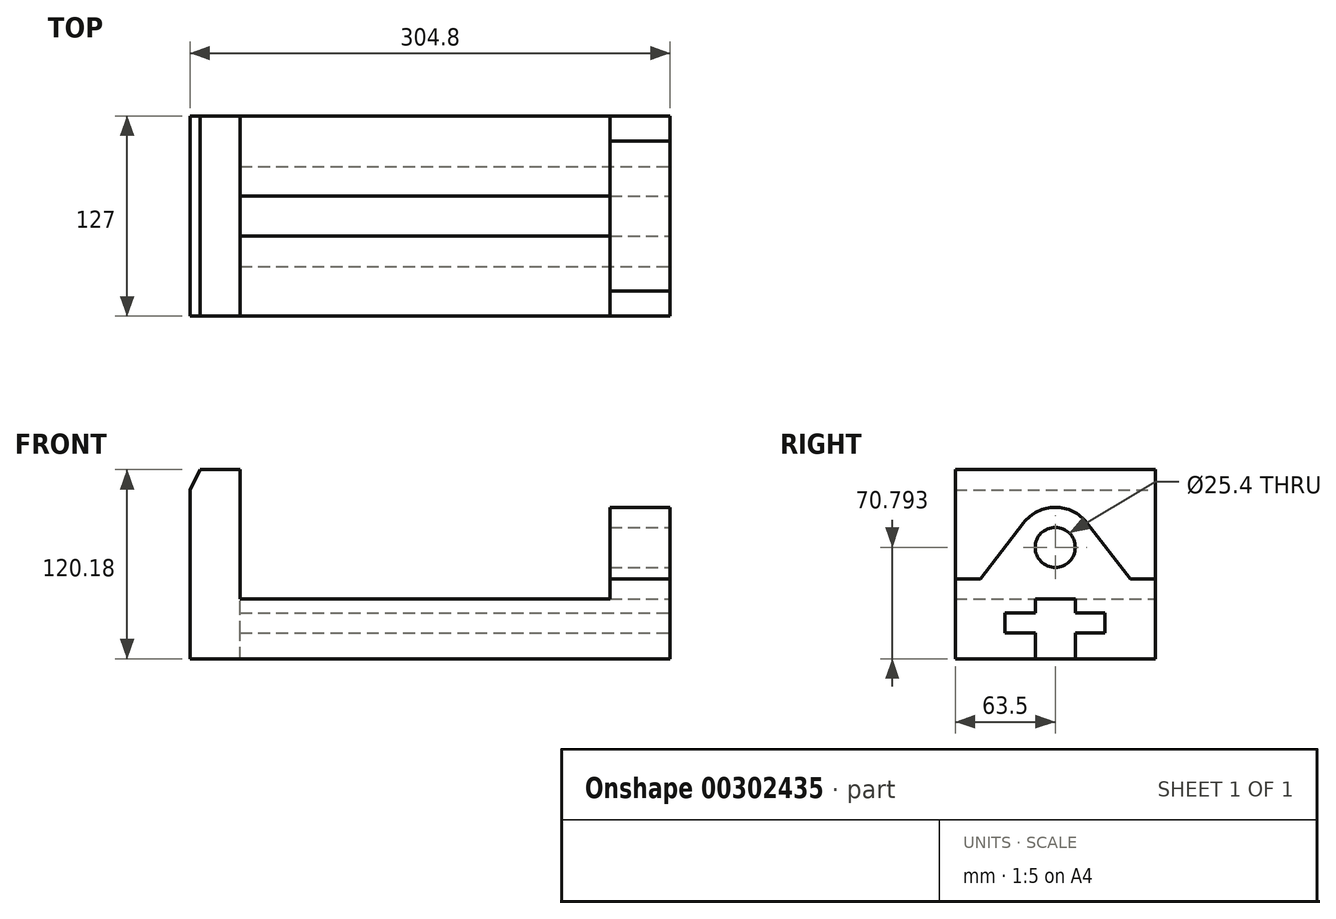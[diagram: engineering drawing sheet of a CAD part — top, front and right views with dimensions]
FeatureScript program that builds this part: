
annotation { "Feature Type Name" : "Feature", "Feature Type Description" : "" }
export const myFeature = defineFeature(function(context is Context, id is Id, definition is map)
    precondition{}
    {
        {
            var Q0;
            Q0=qCreatedBy(makeId("Front.planeOp"),FACE);
            var sketch = newSketch(context, id + "F0", { "sketchPlane" : qUnion([Q0])});
            skLineSegment(sketch, "E0", {"start": v(0, 107.32) * mm, "end": v(0, 0) * mm});
            skLineSegment(sketch, "E1", {"start": v(0, 0) * mm, "end": v(304.8, 0) * mm});
            skLineSegment(sketch, "E2", {"start": v(304.8, 0) * mm, "end": v(304.8, 101.6) * mm});
            skLineSegment(sketch, "E3", {"start": v(304.8, 101.6) * mm, "end": v(266.7, 101.6) * mm});
            skLineSegment(sketch, "E4", {"start": v(266.7, 101.6) * mm, "end": v(266.7, 38.1) * mm});
            skLineSegment(sketch, "E5", {"start": v(266.7, 38.1) * mm, "end": v(31.75, 38.1) * mm});
            skLineSegment(sketch, "E6", {"start": v(31.75, 38.1) * mm, "end": v(31.75, 120.18) * mm});
            skLineSegment(sketch, "E7", {"start": v(31.75, 120.18) * mm, "end": v(6.21, 120.18) * mm});
            skLineSegment(sketch, "E8", {"start": v(6.21, 120.18) * mm, "end": v(0, 107.32) * mm});
            skLineSegment(sketch, "E9", {"start": v(266.7, 60.45) * mm, "end": v(304.8, 60.45) * mm});
            skSolve(sketch);
        }
        {
            var Q0;
            Q0 = qSketchRegion(id + "F0", true);
            extrude(context, id + "F1", {"entities" : qUnion([Q0]), "depth" : 127 * mm});
        }
        {
            var Q0;
            Q0=makeQuery(id+"F1.opExtrude","SWEPT_FACE",FACE,{"disambiguationData":[OSD([sQuery(id+"F0.wireOp",EDGE,"E2")])]});
            var sketch = newSketch(context, id + "F2", { "sketchPlane" : qUnion([Q0])});
            skLineSegment(sketch, "E10", {"start": v(-76.2, 0) * mm, "end": v(-76.2, 16.51) * mm});
            skLineSegment(sketch, "E11", {"start": v(-76.2, 16.51) * mm, "end": v(-95.4, 16.51) * mm});
            skLineSegment(sketch, "E12", {"start": v(-95.4, 16.51) * mm, "end": v(-95.4, 29.21) * mm});
            skLineSegment(sketch, "E13", {"start": v(-95.4, 29.21) * mm, "end": v(-76.2, 29.21) * mm});
            skLineSegment(sketch, "E14", {"start": v(-76.2, 29.21) * mm, "end": v(-76.2, 38.1) * mm});
            skLineSegment(sketch, "E15", {"start": v(-76.2, 38.1) * mm, "end": v(-50.8, 38.1) * mm});
            skLineSegment(sketch, "E16", {"start": v(-50.8, 38.1) * mm, "end": v(-50.8, 29.21) * mm});
            skLineSegment(sketch, "E17", {"start": v(-50.8, 29.21) * mm, "end": v(-31.9, 29.21) * mm});
            skLineSegment(sketch, "E18", {"start": v(-31.9, 29.21) * mm, "end": v(-31.9, 16.51) * mm});
            skLineSegment(sketch, "E19", {"start": v(-31.9, 16.51) * mm, "end": v(-50.8, 16.51) * mm});
            skLineSegment(sketch, "E20", {"start": v(-50.8, 16.51) * mm, "end": v(-50.8, 0) * mm});
            skCircle(sketch, "E21", {"center": v(-63.5, 70.8) * mm, "radius": 12.7 * mm});
            skPoint(sketch, "E21.centerSnap0", {"position": v(-63.5, 38.1) * mm});
            skLineSegment(sketch, "E22", {"start": v(-127, 50.8) * mm, "end": v(-111.13, 50.8) * mm});
            skLineSegment(sketch, "E23", {"start": v(0, 50.8) * mm, "end": v(-15.87, 50.8) * mm});
            skLineSegment(sketch, "E24", {"start": v(-111.12, 50.8) * mm, "end": v(-83.58, 86.35) * mm});
            skLineSegment(sketch, "E25", {"start": v(-15.87, 50.8) * mm, "end": v(-43.42, 86.35) * mm});
            skArc(sketch, "E26", {"start": v(-43.42, 86.35) * mm, "mid": v(-63.5, 96.2) * mm, "end": v(-83.58, 86.35) * mm});
            skSolve(sketch);
        }
        {
            var Q0;
            {var subQ0=sQuery(id+"F2.wireOp",EDGE,"E10");Q0=makeQuery(id+"F2.imprint","IMPRINT",FACE,{"disambiguationData":[TD([[makeQuery(id+"F2.imprint","IMPRINT",EDGE,{"derivedFrom":subQ0}),-1.0]])]});}
            extrude(context, id + "F3", {"entities" : qUnion([Q0]), "operationType" : NewBodyOperationType.REMOVE, "oppositeDirection" : true, "depth" : 273.05 * mm});
        }
        {
            var Q0;
            Q0=makeQuery(id+"F2.imprint","IMPRINT",FACE,{"disambiguationData":[TD([[makeQuery(id+"F2.imprint","IMPRINT",EDGE,{"derivedFrom":sQuery(id+"F2.wireOp",EDGE,"E21")}),1.0]])]});
            var Q1;
            {var subQ4=sQuery(id+"F2.wireOp",EDGE,"E22");Q1=makeQuery(id+"F2.imprint","IMPRINT",FACE,{"disambiguationData":[TD([[makeQuery(id+"F2.imprint","IMPRINT",EDGE,{"derivedFrom":subQ4}),1.0]])]});}
            extrude(context, id + "F4", {"entities" : qUnion([Q0, Q1]), "operationType" : NewBodyOperationType.REMOVE, "oppositeDirection" : true, "depth" : 254 * mm});
        }
    });
